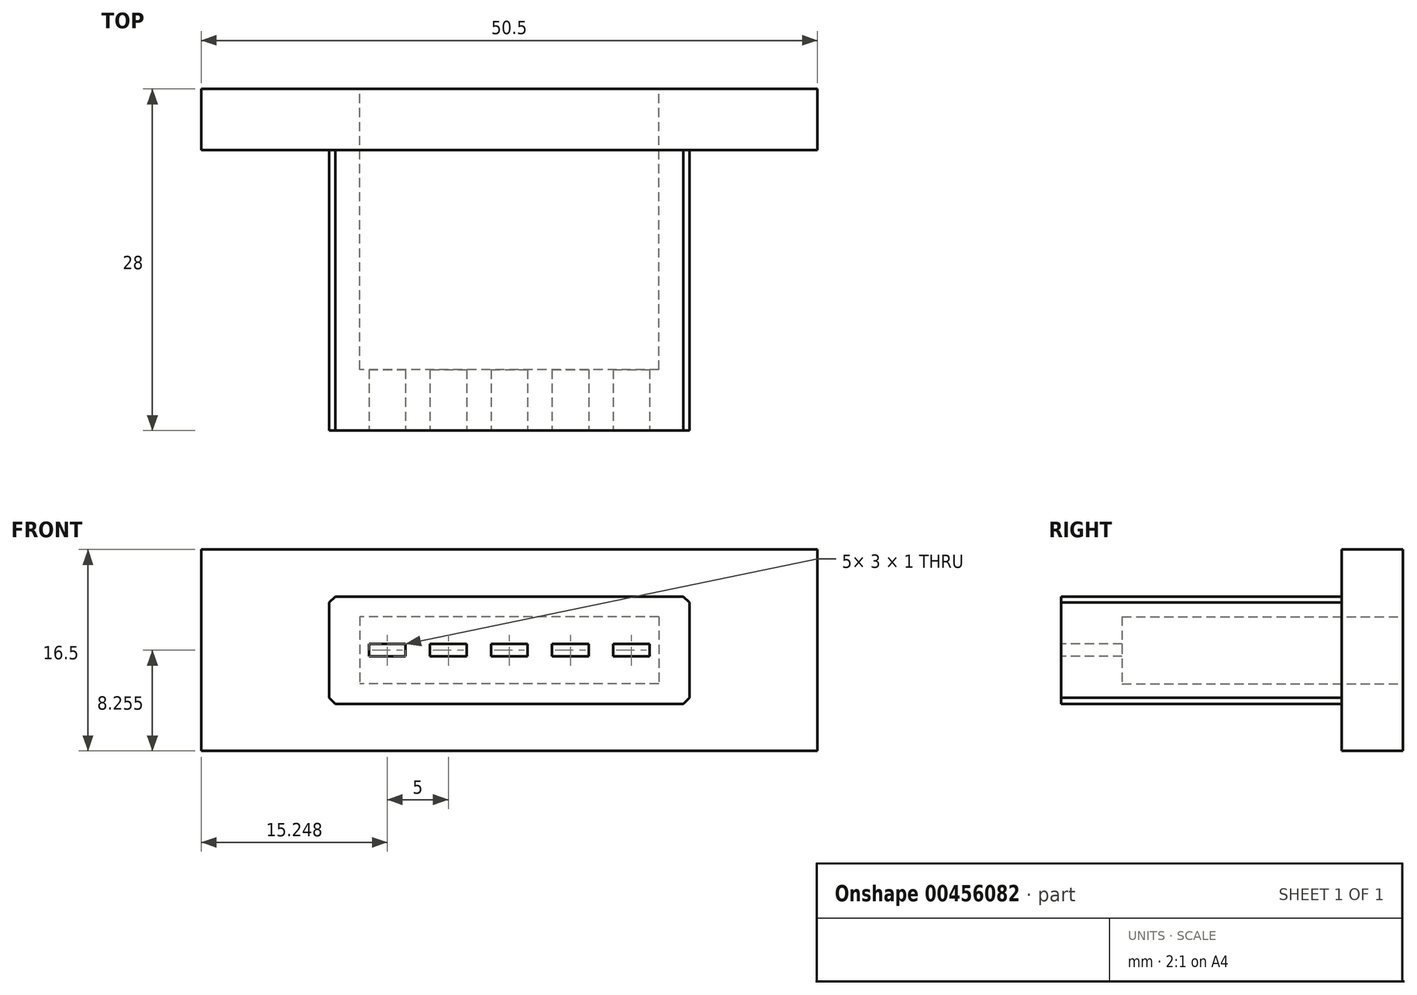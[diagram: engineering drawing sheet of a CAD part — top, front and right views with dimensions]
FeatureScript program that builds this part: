
annotation { "Feature Type Name" : "Feature", "Feature Type Description" : "" }
export const myFeature = defineFeature(function(context is Context, id is Id, definition is map)
    precondition{}
    {
        {
            var Q0;
            Q0=qCreatedBy(makeId("Front.planeOp"),FACE);
            var sketch = newSketch(context, id + "F0", { "sketchPlane" : qUnion([Q0])});
            skLineSegment(sketch, "E0.bottom", {"start": v(-19.5, 10.08) * mm, "end": v(31, 10.08) * mm});
            skLineSegment(sketch, "E0.top", {"start": v(-19.5, -6.42) * mm, "end": v(31, -6.42) * mm});
            skLineSegment(sketch, "E0.left", {"start": v(-19.5, 10.08) * mm, "end": v(-19.5, -6.42) * mm});
            skLineSegment(sketch, "E0.right", {"start": v(31, 10.08) * mm, "end": v(31, -6.42) * mm});
            skSolve(sketch);
        }
        {
            var Q0;
            Q0 = qSketchRegion(id + "F0", true);
            extrude(context, id + "F1", {"entities" : qUnion([Q0]), "depth" : 5 * mm});
        }
        {
            var Q0;
            Q0=makeQuery(id+"F1.opExtrude","CAP_FACE",FACE,{"disambiguationData":[OSD([sQuery(id+"F0.wireOp",EDGE,"E0.bottom"),sQuery(id+"F0.wireOp",EDGE,"E0.top"),sQuery(id+"F0.wireOp",EDGE,"E0.left"),sQuery(id+"F0.wireOp",EDGE,"E0.right")])],"isStart":false});
            var sketch = newSketch(context, id + "F2", { "sketchPlane" : qUnion([Q0])});
            skLineSegment(sketch, "E1.bottom", {"start": v(-9, 6.23) * mm, "end": v(20.5, 6.23) * mm});
            skLineSegment(sketch, "E1.top", {"start": v(-9, -2.57) * mm, "end": v(20.5, -2.57) * mm});
            skLineSegment(sketch, "E1.left", {"start": v(-9, 6.23) * mm, "end": v(-9, -2.57) * mm});
            skLineSegment(sketch, "E1.right", {"start": v(20.5, 6.23) * mm, "end": v(20.5, -2.57) * mm});
            skSolve(sketch);
        }
        {
            var Q0;
            Q0=makeQuery(id+"F2.imprint","IMPRINT",FACE,{"disambiguationData":[TD([[makeQuery(id+"F2.imprint","IMPRINT",EDGE,{"derivedFrom":sQuery(id+"F2.wireOp",EDGE,"E1.bottom")}),-1.0]])]});
            extrude(context, id + "F3", {"entities" : qUnion([Q0]), "operationType" : NewBodyOperationType.ADD, "depth" : 23 * mm});
        }
        {
            var Q0;
            Q0=makeQuery(id+"F3.opExtrude","CAP_FACE",FACE,{"disambiguationData":[OSD([sQuery(id+"F2.wireOp",EDGE,"E1.bottom"),sQuery(id+"F2.wireOp",EDGE,"E1.top"),sQuery(id+"F2.wireOp",EDGE,"E1.left"),sQuery(id+"F2.wireOp",EDGE,"E1.right")])],"isStart":false});
            var sketch = newSketch(context, id + "F4", { "sketchPlane" : qUnion([Q0])});
            skLineSegment(sketch, "E2.bottom", {"start": v(-5.75, 2.33) * mm, "end": v(-2.75, 2.33) * mm});
            skLineSegment(sketch, "E2.top", {"start": v(-5.75, 1.33) * mm, "end": v(-2.75, 1.33) * mm});
            skLineSegment(sketch, "E2.left", {"start": v(-5.75, 2.33) * mm, "end": v(-5.75, 1.33) * mm});
            skLineSegment(sketch, "E2.right", {"start": v(-2.75, 2.33) * mm, "end": v(-2.75, 1.33) * mm});
            skLineSegment(sketch, "E3.bottom", {"start": v(-0.75, 2.33) * mm, "end": v(2.25, 2.33) * mm});
            skLineSegment(sketch, "E3.top", {"start": v(-0.75, 1.33) * mm, "end": v(2.25, 1.33) * mm});
            skLineSegment(sketch, "E3.left", {"start": v(-0.75, 2.33) * mm, "end": v(-0.75, 1.33) * mm});
            skLineSegment(sketch, "E3.right", {"start": v(2.25, 2.33) * mm, "end": v(2.25, 1.33) * mm});
            skLineSegment(sketch, "E4.bottom", {"start": v(4.25, 2.33) * mm, "end": v(7.25, 2.33) * mm});
            skLineSegment(sketch, "E4.top", {"start": v(4.25, 1.33) * mm, "end": v(7.25, 1.33) * mm});
            skLineSegment(sketch, "E4.left", {"start": v(4.25, 2.33) * mm, "end": v(4.25, 1.33) * mm});
            skLineSegment(sketch, "E4.right", {"start": v(7.25, 2.33) * mm, "end": v(7.25, 1.33) * mm});
            skLineSegment(sketch, "E5.bottom", {"start": v(9.25, 2.33) * mm, "end": v(12.25, 2.33) * mm});
            skLineSegment(sketch, "E5.top", {"start": v(9.25, 1.33) * mm, "end": v(12.25, 1.33) * mm});
            skLineSegment(sketch, "E5.left", {"start": v(9.25, 2.33) * mm, "end": v(9.25, 1.33) * mm});
            skLineSegment(sketch, "E5.right", {"start": v(12.25, 2.33) * mm, "end": v(12.25, 1.33) * mm});
            skLineSegment(sketch, "E6.bottom", {"start": v(14.25, 2.33) * mm, "end": v(17.25, 2.33) * mm});
            skLineSegment(sketch, "E6.top", {"start": v(14.25, 1.33) * mm, "end": v(17.25, 1.33) * mm});
            skLineSegment(sketch, "E6.left", {"start": v(14.25, 2.33) * mm, "end": v(14.25, 1.33) * mm});
            skLineSegment(sketch, "E6.right", {"start": v(17.25, 2.33) * mm, "end": v(17.25, 1.33) * mm});
            skSolve(sketch);
        }
        {
            var Q0;
            Q0=makeQuery(id+"F4.imprint","IMPRINT",FACE,{"disambiguationData":[TD([[makeQuery(id+"F4.imprint","IMPRINT",EDGE,{"derivedFrom":sQuery(id+"F4.wireOp",EDGE,"E2.bottom")}),-1.0]])]});
            var Q1;
            Q1=makeQuery(id+"F4.imprint","IMPRINT",FACE,{"disambiguationData":[TD([[makeQuery(id+"F4.imprint","IMPRINT",EDGE,{"derivedFrom":sQuery(id+"F4.wireOp",EDGE,"E3.bottom")}),-1.0]])]});
            var Q2;
            Q2=makeQuery(id+"F4.imprint","IMPRINT",FACE,{"disambiguationData":[TD([[makeQuery(id+"F4.imprint","IMPRINT",EDGE,{"derivedFrom":sQuery(id+"F4.wireOp",EDGE,"E4.bottom")}),-1.0]])]});
            var Q3;
            Q3=makeQuery(id+"F4.imprint","IMPRINT",FACE,{"disambiguationData":[TD([[makeQuery(id+"F4.imprint","IMPRINT",EDGE,{"derivedFrom":sQuery(id+"F4.wireOp",EDGE,"E5.bottom")}),-1.0]])]});
            var Q4;
            Q4=makeQuery(id+"F4.imprint","IMPRINT",FACE,{"disambiguationData":[TD([[makeQuery(id+"F4.imprint","IMPRINT",EDGE,{"derivedFrom":sQuery(id+"F4.wireOp",EDGE,"E6.bottom")}),-1.0]])]});
            extrude(context, id + "F5", {"entities" : qUnion([Q0, Q1, Q2, Q3, Q4]), "operationType" : NewBodyOperationType.REMOVE, "oppositeDirection" : true, "depth" : 28 * mm});
        }
        {
            var Q0;
            Q0=makeQuery(id+"F3.opExtrude","SWEPT_EDGE",EDGE,{"disambiguationData":[OSD([sQuery(id+"F2.wireOp",EDGE,"E1.bottom"),sQuery(id+"F2.wireOp",EDGE,"E1.right")])]});
            var Q1;
            Q1=makeQuery(id+"F3.opExtrude","SWEPT_EDGE",EDGE,{"disambiguationData":[OSD([sQuery(id+"F2.wireOp",EDGE,"E1.bottom"),sQuery(id+"F2.wireOp",EDGE,"E1.left")])]});
            var Q2;
            Q2=makeQuery(id+"F3.opExtrude","SWEPT_EDGE",EDGE,{"disambiguationData":[OSD([sQuery(id+"F2.wireOp",EDGE,"E1.top"),sQuery(id+"F2.wireOp",EDGE,"E1.right")])]});
            var Q3;
            Q3=makeQuery(id+"F3.opExtrude","SWEPT_EDGE",EDGE,{"disambiguationData":[OSD([sQuery(id+"F2.wireOp",EDGE,"E1.top"),sQuery(id+"F2.wireOp",EDGE,"E1.left")])]});
            chamfer(context, id + "F6", {"entities" : qUnion([Q0, Q1, Q2, Q3]), "width" : 0.5 * mm, "tangentPropagation" : true});
        }
        {
            var Q0;
            Q0=makeQuery(id+"F1.opExtrude","CAP_FACE",FACE,{"disambiguationData":[OSD([sQuery(id+"F0.wireOp",EDGE,"E0.bottom"),sQuery(id+"F0.wireOp",EDGE,"E0.top"),sQuery(id+"F0.wireOp",EDGE,"E0.left"),sQuery(id+"F0.wireOp",EDGE,"E0.right")])],"isStart":true});
            var sketch = newSketch(context, id + "F7", { "sketchPlane" : qUnion([Q0])});
            skLineSegment(sketch, "E7.bottom", {"start": v(-18, 4.58) * mm, "end": v(6.5, 4.58) * mm});
            skLineSegment(sketch, "E7.top", {"start": v(-18, -0.92) * mm, "end": v(6.5, -0.92) * mm});
            skLineSegment(sketch, "E7.left", {"start": v(-18, 4.58) * mm, "end": v(-18, -0.92) * mm});
            skLineSegment(sketch, "E7.right", {"start": v(6.5, 4.58) * mm, "end": v(6.5, -0.92) * mm});
            skSolve(sketch);
        }
        {
            var Q0;
            Q0=makeQuery(id+"F7.imprint","IMPRINT",FACE,{"disambiguationData":[TD([[makeQuery(id+"F7.imprint","IMPRINT",EDGE,{"derivedFrom":sQuery(id+"F7.wireOp",EDGE,"E7.bottom")}),-1.0]])]});
            extrude(context, id + "F8", {"entities" : qUnion([Q0]), "operationType" : NewBodyOperationType.REMOVE, "oppositeDirection" : true, "depth" : 23 * mm});
        }
    });
